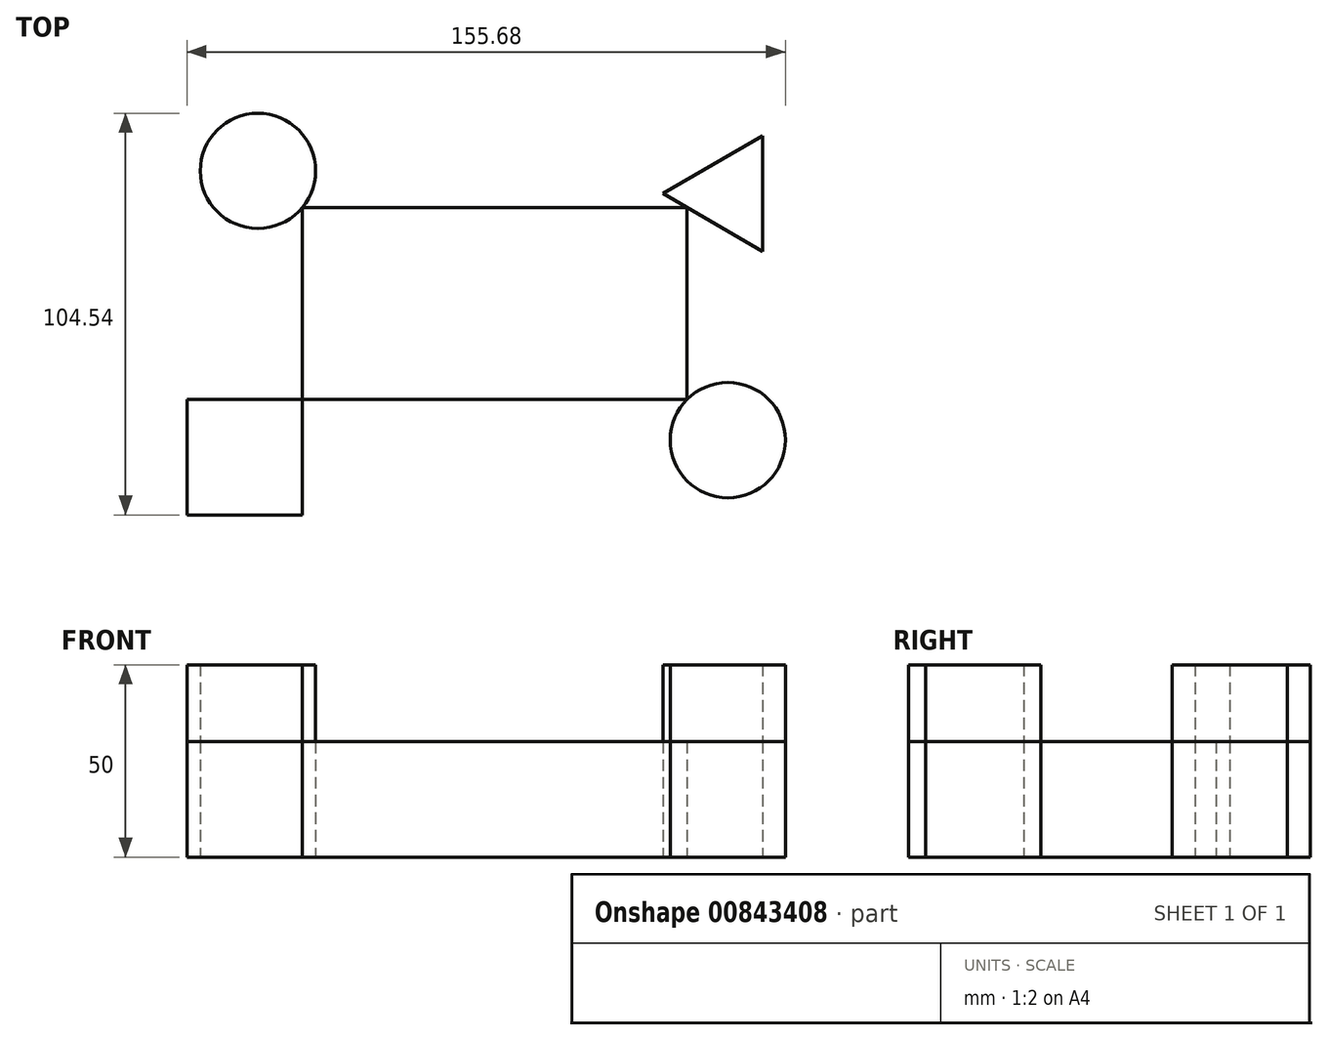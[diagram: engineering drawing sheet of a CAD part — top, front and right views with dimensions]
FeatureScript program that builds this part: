
annotation { "Feature Type Name" : "Feature", "Feature Type Description" : "" }
export const myFeature = defineFeature(function(context is Context, id is Id, definition is map)
    precondition{}
    {
        {
            var Q0;
            Q0=qCreatedBy(makeId("Top.planeOp"),FACE);
            var sketch = newSketch(context, id + "F0", { "sketchPlane" : qUnion([Q0])});
            skLineSegment(sketch, "E0.bottom", {"start": v(-61.3, 27.58) * mm, "end": v(38.7, 27.58) * mm});
            skLineSegment(sketch, "E0.top", {"start": v(-61.3, -22.42) * mm, "end": v(38.7, -22.42) * mm});
            skLineSegment(sketch, "E0.left", {"start": v(-61.3, 27.58) * mm, "end": v(-61.3, -22.42) * mm});
            skLineSegment(sketch, "E0.right", {"start": v(38.7, 27.58) * mm, "end": v(38.7, -22.42) * mm});
            skCircle(sketch, "E1", {"center": v(-72.88, 37.12) * mm, "radius": 15 * mm});
            skPoint(sketch, "E1.second.point", {"position": v(-83.82, 47.38) * mm});
            skPoint(sketch, "E1.third.point", {"position": v(-76.53, 51.67) * mm});
            skCircle(sketch, "E2", {"center": v(49.38, -32.95) * mm, "radius": 15 * mm});
            skPoint(sketch, "E2.second.point", {"position": v(59.35, -44.15) * mm});
            skPoint(sketch, "E2.third.point", {"position": v(63.45, -27.76) * mm});
            skLineSegment(sketch, "E3.bottom", {"start": v(-61.3, -22.42) * mm, "end": v(-91.3, -22.42) * mm});
            skLineSegment(sketch, "E3.top", {"start": v(-61.3, -52.42) * mm, "end": v(-91.3, -52.42) * mm});
            skLineSegment(sketch, "E3.left", {"start": v(-61.3, -22.42) * mm, "end": v(-61.3, -52.42) * mm});
            skLineSegment(sketch, "E3.right", {"start": v(-91.3, -22.42) * mm, "end": v(-91.3, -52.42) * mm});
            skLineSegment(sketch, "E4", {"start": v(32.46, 31.18) * mm, "end": v(58.44, 16.18) * mm});
            skLineSegment(sketch, "E5", {"start": v(58.44, 16.18) * mm, "end": v(58.44, 46.18) * mm});
            skLineSegment(sketch, "E6", {"start": v(58.44, 46.18) * mm, "end": v(32.46, 31.18) * mm});
            skSolve(sketch);
        }
        {
            var Q0;
            Q0 = qSketchRegion(id + "F0", true);
            extrude(context, id + "F1", {"entities" : qUnion([Q0]), "depth" : 30 * mm, "offsetDistance" : 25.4 * mm});
        }
        {
            var Q0;
            Q0=makeQuery(id+"F1.opExtrude","CAP_FACE",FACE,{"disambiguationData":[OSD([sQuery(id+"F0.wireOp",EDGE,"E4"),sQuery(id+"F0.wireOp",EDGE,"E5"),sQuery(id+"F0.wireOp",EDGE,"E6")])],"isStart":false});
            var Q1;
            Q1=makeQuery(id+"F1.opExtrude","CAP_FACE",FACE,{"disambiguationData":[OSD([sQuery(id+"F0.wireOp",EDGE,"E2")])],"isStart":false});
            var Q2;
            Q2=makeQuery(id+"F1.opExtrude","CAP_FACE",FACE,{"disambiguationData":[OSD([sQuery(id+"F0.wireOp",EDGE,"E3.bottom"),sQuery(id+"F0.wireOp",EDGE,"E3.top"),sQuery(id+"F0.wireOp",EDGE,"E3.left"),sQuery(id+"F0.wireOp",EDGE,"E3.right")])],"isStart":false});
            var Q3;
            Q3=makeQuery(id+"F1.opExtrude","CAP_FACE",FACE,{"disambiguationData":[OSD([sQuery(id+"F0.wireOp",EDGE,"E1")])],"isStart":false});
            extrude(context, id + "F2", {"entities" : qUnion([Q0, Q1, Q2, Q3]), "depth" : 20 * mm, "offsetDistance" : 25.4 * mm});
        }
    });
